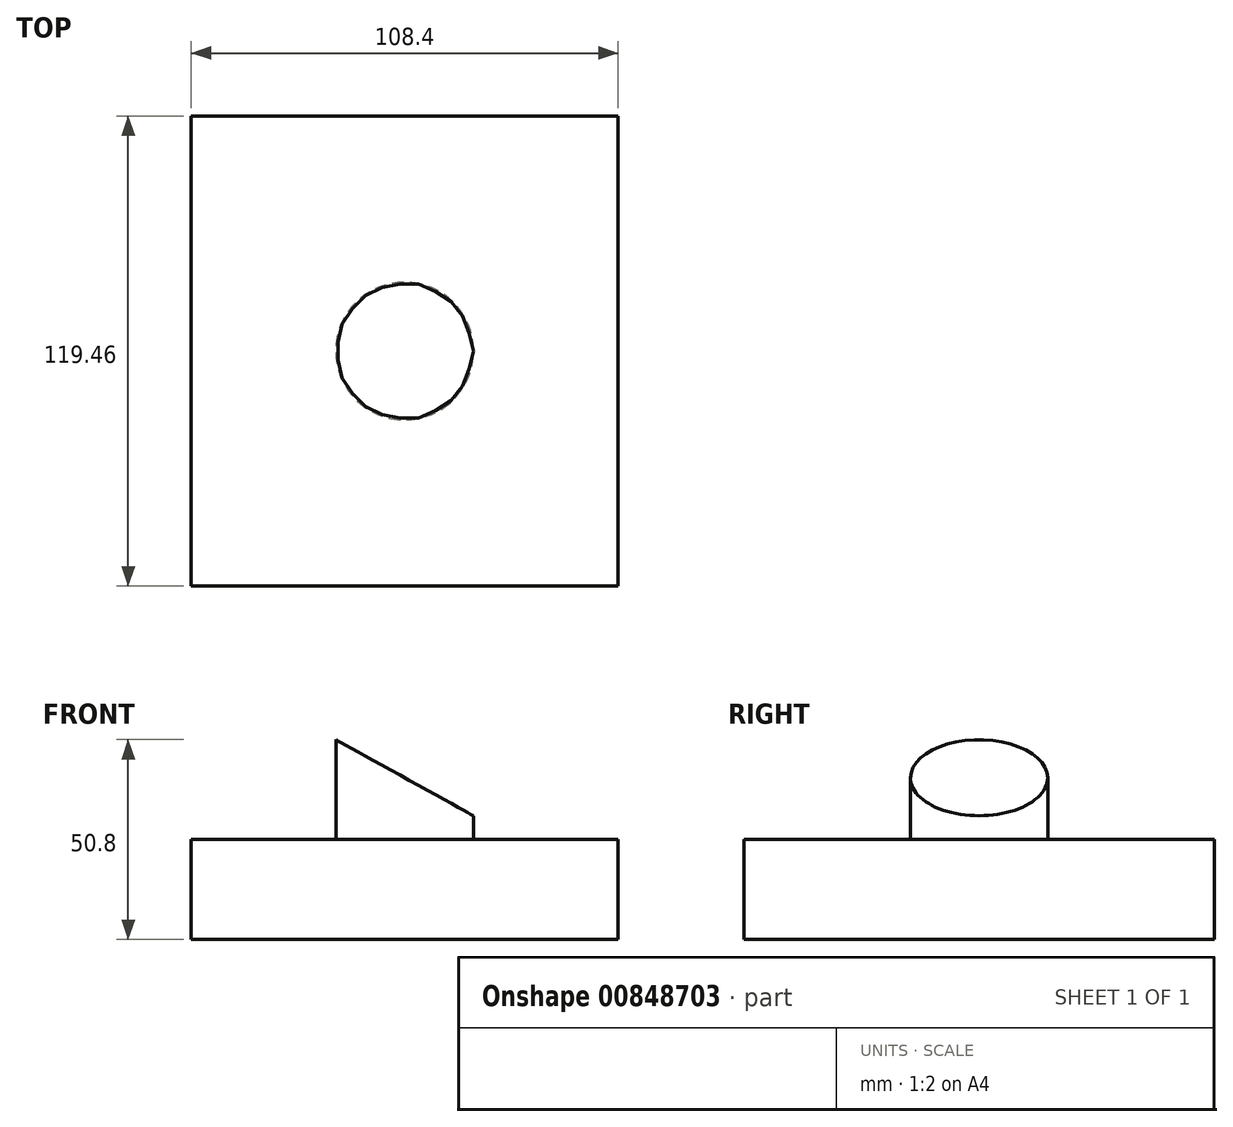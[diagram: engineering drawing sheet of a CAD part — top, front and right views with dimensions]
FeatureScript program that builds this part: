
annotation { "Feature Type Name" : "Feature", "Feature Type Description" : "" }
export const myFeature = defineFeature(function(context is Context, id is Id, definition is map)
    precondition{}
    {
        {
            var Q0;
            Q0=qCreatedBy(makeId("Top.planeOp"),FACE);
            var sketch = newSketch(context, id + "F0", { "sketchPlane" : qUnion([Q0])});
            skLineSegment(sketch, "E0.bottom", {"start": v(54.2, -59.73) * mm, "end": v(-54.2, -59.73) * mm});
            skLineSegment(sketch, "E0.top", {"start": v(54.2, 59.73) * mm, "end": v(-54.2, 59.73) * mm});
            skLineSegment(sketch, "E0.left", {"start": v(54.2, -59.73) * mm, "end": v(54.2, 59.73) * mm});
            skLineSegment(sketch, "E0.right", {"start": v(-54.2, -59.73) * mm, "end": v(-54.2, 59.73) * mm});
            skPoint(sketch, "E0.middle", {"position": v(0, 0) * mm});
            skSolve(sketch);
        }
        {
            var Q0;
            Q0 = qSketchRegion(id + "F0", true);
            extrude(context, id + "F1", {"entities" : qUnion([Q0]), "depth" : 25.4 * mm, "offsetDistance" : 25.4 * mm});
        }
        {
            var Q0;
            Q0=makeQuery(id+"F1.opExtrude","CAP_FACE",FACE,{"disambiguationData":[OSD([sQuery(id+"F0.wireOp",EDGE,"E0.bottom"),sQuery(id+"F0.wireOp",EDGE,"E0.top"),sQuery(id+"F0.wireOp",EDGE,"E0.left"),sQuery(id+"F0.wireOp",EDGE,"E0.right")])],"isStart":false});
            var sketch = newSketch(context, id + "F2", { "sketchPlane" : qUnion([Q0])});
            skCircle(sketch, "E1", {"center": v(0, 0) * mm, "radius": 17.47 * mm});
            skSolve(sketch);
        }
        {
            var Q0;
            Q0 = qSketchRegion(id + "F2", true);
            extrude(context, id + "F3", {"entities" : qUnion([Q0]), "operationType" : NewBodyOperationType.ADD, "depth" : 25.4 * mm, "offsetDistance" : 25.4 * mm});
        }
        {
            var Q0;
            Q0=makeQuery(id+"F1.opExtrude","SWEPT_FACE",FACE,{"disambiguationData":[OSD([sQuery(id+"F0.wireOp",EDGE,"E0.bottom")])]});
            var sketch = newSketch(context, id + "F4", { "sketchPlane" : qUnion([Q0])});
            skLineSegment(sketch, "E2.0", {"start": v(-17.47, 50.8) * mm, "end": v(17.47, 50.8) * mm});
            skLineSegment(sketch, "E3", {"start": v(-17.47, 50.8) * mm, "end": v(17.47, 31.46) * mm});
            skLineSegment(sketch, "E4", {"start": v(17.47, 31.46) * mm, "end": v(17.47, 50.8) * mm});
            skSolve(sketch);
        }
        {
            var Q0;
            Q0 = qSketchRegion(id + "F4", true);
            extrude(context, id + "F5", {"entities" : qUnion([Q0]), "operationType" : NewBodyOperationType.REMOVE, "endBound" : BoundingType.THROUGH_ALL, "oppositeDirection" : true, "depth" : 25.4 * mm, "offsetDistance" : 25.4 * mm});
        }
    });
